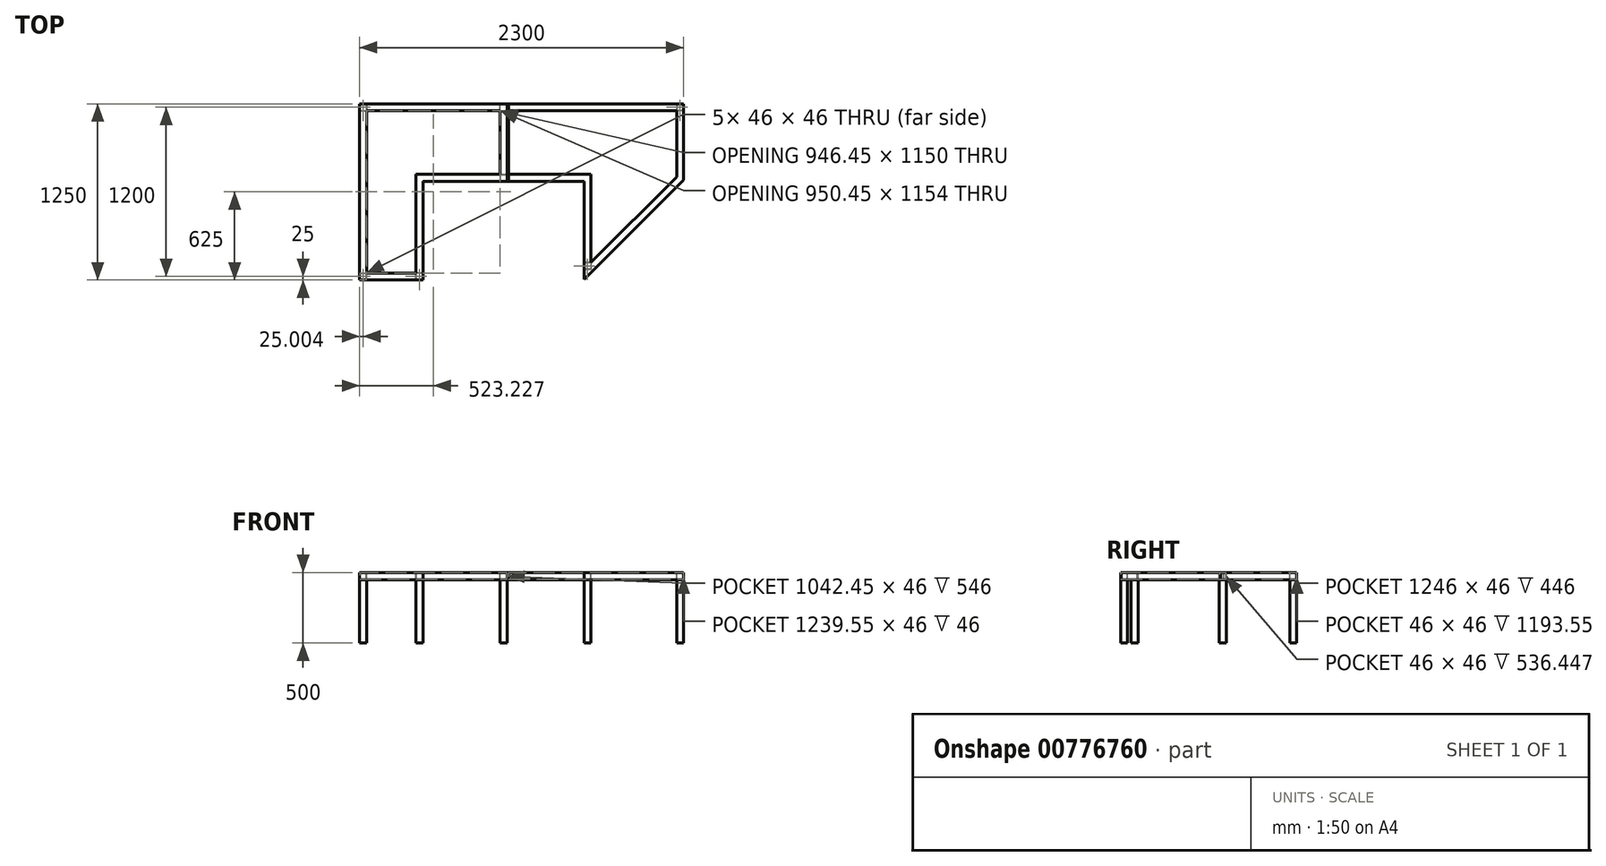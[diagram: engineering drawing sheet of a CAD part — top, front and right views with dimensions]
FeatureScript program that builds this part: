
annotation { "Feature Type Name" : "Feature", "Feature Type Description" : "" }
export const myFeature = defineFeature(function(context is Context, id is Id, definition is map)
    precondition{}
    {
        {
            var Q0;
            Q0=qCreatedBy(makeId("Top.planeOp"),FACE);
            var sketch = newSketch(context, id + "F0", { "sketchPlane" : qUnion([Q0])});
            skLineSegment(sketch, "E0.top", {"start": v(-571.45, -975) * mm, "end": v(-1021.45, -975) * mm});
            skLineSegment(sketch, "E0.left", {"start": v(-571.45, -275) * mm, "end": v(-571.45, -975) * mm});
            skLineSegment(sketch, "E0.right", {"start": v(-1021.45, 275) * mm, "end": v(-1021.45, -975) * mm});
            skLineSegment(sketch, "E1.right", {"start": v(1278.55, 275) * mm, "end": v(1278.55, -265) * mm});
            skLineSegment(sketch, "E2", {"start": v(1278.55, -265) * mm, "end": v(571.45, -972.1) * mm});
            skLineSegment(sketch, "E3", {"start": v(571.45, -972.1) * mm, "end": v(571.45, -275) * mm});
            skLineSegment(sketch, "E4", {"start": v(1278.55, 275) * mm, "end": v(-1021.45, 275) * mm});
            skLineSegment(sketch, "E5", {"start": v(-571.45, -275) * mm, "end": v(571.45, -275) * mm});
            skLineSegment(sketch, "E6", {"start": v(35, -275) * mm, "end": v(35, 275) * mm});
            skLineSegment(sketch, "E7", {"start": v(0, 250) * mm, "end": v(0, -250) * mm, "construction": true});
            skLineSegment(sketch, "E8", {"start": v(25, 275) * mm, "end": v(25, -275) * mm});
            skLineSegment(sketch, "E9.0", {"start": v(621.45, -851.4) * mm, "end": v(621.45, -225) * mm});
            skLineSegment(sketch, "E9.1", {"start": v(1228.55, -244.29) * mm, "end": v(621.45, -851.4) * mm});
            skLineSegment(sketch, "E9.2", {"start": v(1228.55, 225) * mm, "end": v(1228.55, -244.29) * mm});
            skLineSegment(sketch, "E10.0", {"start": v(-621.45, -225) * mm, "end": v(-621.45, -925) * mm});
            skLineSegment(sketch, "E10.1", {"start": v(-621.45, -925) * mm, "end": v(-971.45, -925) * mm});
            skLineSegment(sketch, "E10.2", {"start": v(-971.45, 225) * mm, "end": v(-971.45, -925) * mm});
            skLineSegment(sketch, "E11", {"start": v(1228.55, 225) * mm, "end": v(35, 225) * mm});
            skLineSegment(sketch, "E12", {"start": v(35, -225) * mm, "end": v(621.45, -225) * mm});
            skLineSegment(sketch, "E13", {"start": v(-621.45, -225) * mm, "end": v(-25, -225) * mm});
            skLineSegment(sketch, "E14", {"start": v(-25, -225) * mm, "end": v(-25, 225) * mm});
            skLineSegment(sketch, "E15.trimOffspring", {"start": v(-25, 225) * mm, "end": v(-971.45, 225) * mm});
            skLineSegment(sketch, "E16", {"start": v(25, 275) * mm, "end": v(-25, 225) * mm});
            skLineSegment(sketch, "E17", {"start": v(-25, -225) * mm, "end": v(25, -275) * mm});
            skLineSegment(sketch, "E18", {"start": v(-621.45, -925) * mm, "end": v(-571.45, -975) * mm});
            skLineSegment(sketch, "E19", {"start": v(-971.45, -925) * mm, "end": v(-1021.45, -975) * mm});
            skLineSegment(sketch, "E20", {"start": v(-571.45, -275) * mm, "end": v(-621.45, -225) * mm});
            skLineSegment(sketch, "E21", {"start": v(-971.45, 225) * mm, "end": v(-1021.45, 275) * mm});
            skLineSegment(sketch, "E22", {"start": v(621.45, -225) * mm, "end": v(571.45, -275) * mm});
            skLineSegment(sketch, "E23", {"start": v(621.45, -851.4) * mm, "end": v(571.45, -901.4) * mm});
            skLineSegment(sketch, "E24", {"start": v(1278.55, -265) * mm, "end": v(1228.55, -244.29) * mm});
            skLineSegment(sketch, "E25", {"start": v(1278.55, 275) * mm, "end": v(1228.55, 225) * mm});
            skSolve(sketch);
        }
        {
            var Q0;
            {var subQ4=sQuery(id+"F0.wireOp",EDGE,"E11");Q0=makeQuery(id+"F0.imprint","IMPRINT",FACE,{"disambiguationData":[TD([[makeQuery(id+"F0.imprint","IMPRINT",EDGE,{"derivedFrom":subQ4}),-1.0]])]});}
            var Q1;
            {var subQ4=sQuery(id+"F0.wireOp",EDGE,"E12");Q1=makeQuery(id+"F0.imprint","IMPRINT",FACE,{"disambiguationData":[TD([[makeQuery(id+"F0.imprint","IMPRINT",EDGE,{"derivedFrom":subQ4}),-1.0]])]});}
            var Q2;
            Q2=makeQuery(id+"F0.imprint","IMPRINT",FACE,{"disambiguationData":[TD([[makeQuery(id+"F0.imprint","IMPRINT",EDGE,{"derivedFrom":sQuery(id+"F0.wireOp",EDGE,"E1.right")}),-1.0]])]});
            var Q3;
            {var subQ2=sQuery(id+"F0.wireOp",EDGE,"E2");Q3=makeQuery(id+"F0.imprint","IMPRINT",FACE,{"disambiguationData":[TD([[makeQuery(id+"F0.imprint","IMPRINT",EDGE,{"derivedFrom":subQ2}),-1.0]])]});}
            var Q4;
            Q4=makeQuery(id+"F0.imprint","IMPRINT",FACE,{"disambiguationData":[TD([[makeQuery(id+"F0.imprint","IMPRINT",EDGE,{"derivedFrom":sQuery(id+"F0.wireOp",EDGE,"E9.0")}),1.0]])]});
            extrude(context, id + "F1", {"entities" : qUnion([Q0, Q1, Q2, Q3, Q4]), "oppositeDirection" : true, "depth" : 50 * mm, "offsetDistance" : 25 * mm});
        }
        {
            var Q0;
            Q0=makeQuery(id+"F0.imprint","IMPRINT",FACE,{"disambiguationData":[TD([[makeQuery(id+"F0.imprint","IMPRINT",EDGE,{"derivedFrom":sQuery(id+"F0.wireOp",EDGE,"E0.right")}),1.0]])]});
            var Q1;
            Q1=makeQuery(id+"F0.imprint","IMPRINT",FACE,{"disambiguationData":[TD([[makeQuery(id+"F0.imprint","IMPRINT",EDGE,{"derivedFrom":sQuery(id+"F0.wireOp",EDGE,"E0.top")}),-1.0]])]});
            var Q2;
            Q2=makeQuery(id+"F0.imprint","IMPRINT",FACE,{"disambiguationData":[TD([[makeQuery(id+"F0.imprint","IMPRINT",EDGE,{"derivedFrom":sQuery(id+"F0.wireOp",EDGE,"E0.left")}),-1.0]])]});
            var Q3;
            Q3=makeQuery(id+"F0.imprint","IMPRINT",FACE,{"disambiguationData":[TD([[makeQuery(id+"F0.imprint","IMPRINT",EDGE,{"derivedFrom":sQuery(id+"F0.wireOp",EDGE,"E15.trimOffspring")}),-1.0]])]});
            var Q4;
            Q4=makeQuery(id+"F0.imprint","IMPRINT",FACE,{"disambiguationData":[TD([[makeQuery(id+"F0.imprint","IMPRINT",EDGE,{"derivedFrom":sQuery(id+"F0.wireOp",EDGE,"E13")}),-1.0]])]});
            var Q5;
            Q5=makeQuery(id+"F0.imprint","IMPRINT",FACE,{"disambiguationData":[TD([[makeQuery(id+"F0.imprint","IMPRINT",EDGE,{"derivedFrom":sQuery(id+"F0.wireOp",EDGE,"E8")}),-1.0]])]});
            extrude(context, id + "F2", {"entities" : qUnion([Q0, Q1, Q2, Q3, Q4, Q5]), "oppositeDirection" : true, "depth" : 50 * mm, "offsetDistance" : 25 * mm});
        }
        {
            var Q0;
            {var subQ5=sQuery(id+"F0.wireOp",EDGE,"E8");Q0=makeQuery(id+"F0.imprint","IMPRINT",FACE,{"disambiguationData":[TD([[makeQuery(id+"F0.imprint","IMPRINT",EDGE,{"derivedFrom":subQ5}),1.0]])]});}
            extrude(context, id + "F3", {"entities" : qUnion([Q0]), "oppositeDirection" : true, "depth" : 50 * mm, "offsetDistance" : 25 * mm});
        }
        {
            var Q0;
            Q0=makeQuery(id+"F2.opExtrude","SWEPT_FACE",FACE,{"disambiguationData":[OSD([sQuery(id+"F0.wireOp",EDGE,"2A5xBHzc-K11I-RF4C-uFUW-yK5MyYlXpvJs")])]});
            var Q1;
            Q1=makeQuery(id+"F2.opExtrude","SWEPT_FACE",FACE,{"disambiguationData":[OSD([sQuery(id+"F0.wireOp",EDGE,"euzSzvIf-zb11-oeAi-6vT1-MCLPW0OJACnm")])]});
            var Q2;
            Q2=makeQuery(id+"F2.opExtrude","SWEPT_FACE",FACE,{"disambiguationData":[OSD([sQuery(id+"F0.wireOp",EDGE,"GaZW1oPM-7css-87Zt-WlsF-Pj7CSG2FI9am")])]});
            var Q3;
            Q3=makeQuery(id+"F2.opExtrude","SWEPT_FACE",FACE,{"disambiguationData":[OSD([sQuery(id+"F0.wireOp",EDGE,"sEP72Xz7-jys3-R5h0-IGae-Pih6YAF2AQWA")])]});
            var Q4;
            Q4=makeQuery(id+"F2.opExtrude","SWEPT_FACE",FACE,{"disambiguationData":[OSD([sQuery(id+"F0.wireOp",EDGE,"c1XjSD7W-lne4-ik7T-Z6My-GW0DLpmjkOK7")])]});
            var Q5;
            Q5=makeQuery(id+"F2.opExtrude","SWEPT_FACE",FACE,{"disambiguationData":[OSD([sQuery(id+"F0.wireOp",EDGE,"E3")])]});
            var Q6;
            Q6=makeQuery(id+"F2.opExtrude","SWEPT_FACE",FACE,{"disambiguationData":[OSD([sQuery(id+"F0.wireOp",EDGE,"Wdln1U8m-EFWw-qeqF-QT6C-txq9QpAb5bMw")])]});
            var Q7;
            Q7=makeQuery(id+"F2.opExtrude","SWEPT_FACE",FACE,{"disambiguationData":[OSD([sQuery(id+"F0.wireOp",EDGE,"AmBgJv7p-42l0-yFrp-UsyM-nx3i3Yf4QRB6")])]});
            var Q8;
            Q8=makeQuery(id+"F2.opExtrude","SWEPT_FACE",FACE,{"disambiguationData":[OSD([sQuery(id+"F0.wireOp",EDGE,"OMlm4TEm-4dLt-MTcu-9hLO-nY8Iuq9vEE24")])]});
            var Q9;
            Q9=makeQuery(id+"F2.opExtrude","SWEPT_FACE",FACE,{"disambiguationData":[OSD([sQuery(id+"F0.wireOp",EDGE,"wsWtQ9dq-29bv-YeLY-ytrv-cSZXrYwj46Cy")])]});
            var Q10;
            Q10=makeQuery(id+"F2.opExtrude","SWEPT_FACE",FACE,{"disambiguationData":[OSD([sQuery(id+"F0.wireOp",EDGE,"UwJ4Ktt8-JkZr-7fMy-kYLK-IwmRaqzIre9T")])]});
            var Q11;
            Q11=makeQuery(id+"F2.opExtrude","SWEPT_FACE",FACE,{"disambiguationData":[OSD([sQuery(id+"F0.wireOp",EDGE,"jgCBQ05M-ki6p-DAOy-uykI-KBMVmP0mj9T2")])]});
            var Q12;
            Q12=makeQuery(id+"F2.opExtrude","SWEPT_BODY",BODY,{"disambiguationData":[OSD([sQuery(id+"F0.wireOp",EDGE,"E0.top"),sQuery(id+"F0.wireOp",EDGE,"E0.left"),sQuery(id+"F0.wireOp",EDGE,"E0.right"),sQuery(id+"F0.wireOp",EDGE,"E4"),sQuery(id+"F0.wireOp",EDGE,"E5"),sQuery(id+"F0.wireOp",EDGE,"E8"),sQuery(id+"F0.wireOp",EDGE,"E10.0"),sQuery(id+"F0.wireOp",EDGE,"E10.1"),sQuery(id+"F0.wireOp",EDGE,"E10.2"),sQuery(id+"F0.wireOp",EDGE,"E13"),sQuery(id+"F0.wireOp",EDGE,"E14"),sQuery(id+"F0.wireOp",EDGE,"E15.trimOffspring")])]});
            var Q13;
            Q13=makeQuery(id+"F1.opExtrude","SWEPT_BODY",BODY,{"disambiguationData":[OSD([sQuery(id+"F0.wireOp",EDGE,"E1.right"),sQuery(id+"F0.wireOp",EDGE,"E2"),sQuery(id+"F0.wireOp",EDGE,"E3"),sQuery(id+"F0.wireOp",EDGE,"E4"),sQuery(id+"F0.wireOp",EDGE,"E5"),sQuery(id+"F0.wireOp",EDGE,"E6"),sQuery(id+"F0.wireOp",EDGE,"E9.0"),sQuery(id+"F0.wireOp",EDGE,"E9.1"),sQuery(id+"F0.wireOp",EDGE,"E9.2"),sQuery(id+"F0.wireOp",EDGE,"E11"),sQuery(id+"F0.wireOp",EDGE,"E12")])]});
            shell(context, id + "F4", {"isHollow" : true, "entities" : qUnion([Q0, Q1, Q2, Q3, Q4, Q5, Q6, Q7, Q8, Q9, Q10, Q11]), "parts" : qUnion([Q12, Q13]), "thickness" : 2 * mm});
        }
        {
            var Q0;
            Q0=makeQuery(id+"F1.opExtrude","CAP_FACE",FACE,{"disambiguationData":[OSD([sQuery(id+"F0.wireOp",EDGE,"E0.top"),sQuery(id+"F0.wireOp",EDGE,"E0.left"),sQuery(id+"F0.wireOp",EDGE,"E0.right"),sQuery(id+"F0.wireOp",EDGE,"E1.bottom"),sQuery(id+"F0.wireOp",EDGE,"E1.right"),sQuery(id+"F0.wireOp",EDGE,"E2"),sQuery(id+"F0.wireOp",EDGE,"E3"),sQuery(id+"F0.wireOp",EDGE,"E4"),sQuery(id+"F0.wireOp",EDGE,"3MHuuK1R-XM8M-TEry-PjCO-C2Ca8WDOHeh9"),sQuery(id+"F0.wireOp",EDGE,"E5"),sQuery(id+"F0.wireOp",EDGE,"ef3f4d72-5e47-419f-9294-d8863ce435e2.0"),sQuery(id+"F0.wireOp",EDGE,"ef3f4d72-5e47-419f-9294-d8863ce435e2.1"),sQuery(id+"F0.wireOp",EDGE,"ef3f4d72-5e47-419f-9294-d8863ce435e2.2"),sQuery(id+"F0.wireOp",EDGE,"ef3f4d72-5e47-419f-9294-d8863ce435e2.3"),sQuery(id+"F0.wireOp",EDGE,"ef3f4d72-5e47-419f-9294-d8863ce435e2.4"),sQuery(id+"F0.wireOp",EDGE,"ef3f4d72-5e47-419f-9294-d8863ce435e2.5"),sQuery(id+"F0.wireOp",EDGE,"93901ade-92e2-49f1-bb5c-9fd08a6a9788.0"),sQuery(id+"F0.wireOp",EDGE,"93901ade-92e2-49f1-bb5c-9fd08a6a9788.1"),sQuery(id+"F0.wireOp",EDGE,"93901ade-92e2-49f1-bb5c-9fd08a6a9788.2"),sQuery(id+"F0.wireOp",EDGE,"93901ade-92e2-49f1-bb5c-9fd08a6a9788.3"),sQuery(id+"F0.wireOp",EDGE,"93901ade-92e2-49f1-bb5c-9fd08a6a9788.4"),sQuery(id+"F0.wireOp",EDGE,"93901ade-92e2-49f1-bb5c-9fd08a6a9788.5")])],"isStart":false});
            var sketch = newSketch(context, id + "F5", { "sketchPlane" : qUnion([Q0])});
            skLineSegment(sketch, "E26.bottom", {"start": v(-1021.45, 975) * mm, "end": v(-971.45, 975) * mm});
            skLineSegment(sketch, "E26.top", {"start": v(-1021.45, 925) * mm, "end": v(-971.45, 925) * mm});
            skLineSegment(sketch, "E26.left", {"start": v(-1021.45, 975) * mm, "end": v(-1021.45, 925) * mm});
            skLineSegment(sketch, "E26.right", {"start": v(-971.45, 975) * mm, "end": v(-971.45, 925) * mm});
            skLineSegment(sketch, "E27.bottom", {"start": v(-1021.45, -275) * mm, "end": v(-971.45, -275) * mm});
            skLineSegment(sketch, "E27.top", {"start": v(-1021.45, -225) * mm, "end": v(-971.45, -225) * mm});
            skLineSegment(sketch, "E27.left", {"start": v(-1021.45, -275) * mm, "end": v(-1021.45, -225) * mm});
            skLineSegment(sketch, "E27.right", {"start": v(-971.45, -275) * mm, "end": v(-971.45, -225) * mm});
            skLineSegment(sketch, "E28.bottom", {"start": v(1278.55, -275) * mm, "end": v(1228.55, -275) * mm});
            skLineSegment(sketch, "E28.top", {"start": v(1278.55, -225) * mm, "end": v(1228.55, -225) * mm});
            skLineSegment(sketch, "E28.left", {"start": v(1278.55, -275) * mm, "end": v(1278.55, -225) * mm});
            skLineSegment(sketch, "E28.right", {"start": v(1228.55, -275) * mm, "end": v(1228.55, -225) * mm});
            skLineSegment(sketch, "E29.bottom", {"start": v(621.45, 851.4) * mm, "end": v(571.45, 851.4) * mm});
            skLineSegment(sketch, "E29.top", {"start": v(621.45, 901.4) * mm, "end": v(571.45, 901.4) * mm});
            skLineSegment(sketch, "E29.left", {"start": v(621.45, 851.4) * mm, "end": v(621.45, 901.4) * mm});
            skLineSegment(sketch, "E29.right", {"start": v(571.45, 851.4) * mm, "end": v(571.45, 901.4) * mm});
            skPoint(sketch, "E30.0", {"position": v(-971.45, 925) * mm});
            skPoint(sketch, "E31.0", {"position": v(-1021.45, 975) * mm});
            skPoint(sketch, "E32.0", {"position": v(-1021.45, -275) * mm});
            skPoint(sketch, "E33.0", {"position": v(-971.45, -225) * mm});
            skPoint(sketch, "E34.0", {"position": v(-571.45, 975) * mm});
            skPoint(sketch, "E35.0", {"position": v(-621.45, 925) * mm});
            skLineSegment(sketch, "E36.bottom", {"start": v(-571.45, 975) * mm, "end": v(-621.45, 975) * mm});
            skLineSegment(sketch, "E36.top", {"start": v(-571.45, 925) * mm, "end": v(-621.45, 925) * mm});
            skLineSegment(sketch, "E36.left", {"start": v(-571.45, 975) * mm, "end": v(-571.45, 925) * mm});
            skLineSegment(sketch, "E36.right", {"start": v(-621.45, 975) * mm, "end": v(-621.45, 925) * mm});
            skPoint(sketch, "E37.0", {"position": v(1228.55, -225) * mm});
            skPoint(sketch, "E38.0", {"position": v(1278.55, -275) * mm});
            skPoint(sketch, "E39.0", {"position": v(621.45, 851.4) * mm});
            skLineSegment(sketch, "E40.0", {"start": v(571.45, 972.1) * mm, "end": v(571.45, 275) * mm, "construction": true});
            skPoint(sketch, "E41.0", {"position": v(-25, 225) * mm});
            skPoint(sketch, "E42.0", {"position": v(25, 275) * mm});
            skPoint(sketch, "E43.0", {"position": v(-25, -225) * mm});
            skPoint(sketch, "E44.0", {"position": v(25, -275) * mm});
            skLineSegment(sketch, "E45.bottom", {"start": v(-25, 225) * mm, "end": v(25, 225) * mm});
            skLineSegment(sketch, "E45.top", {"start": v(-25, 275) * mm, "end": v(25, 275) * mm});
            skLineSegment(sketch, "E45.left", {"start": v(-25, 225) * mm, "end": v(-25, 275) * mm});
            skLineSegment(sketch, "E45.right", {"start": v(25, 225) * mm, "end": v(25, 275) * mm});
            skLineSegment(sketch, "E46.bottom", {"start": v(-25, -225) * mm, "end": v(25, -225) * mm});
            skLineSegment(sketch, "E46.top", {"start": v(-25, -275) * mm, "end": v(25, -275) * mm});
            skLineSegment(sketch, "E46.left", {"start": v(-25, -225) * mm, "end": v(-25, -275) * mm});
            skLineSegment(sketch, "E46.right", {"start": v(25, -225) * mm, "end": v(25, -275) * mm});
            skSolve(sketch);
        }
        {
            var Q0;
            Q0 = qSketchRegion(id + "F5", true);
            extrude(context, id + "F6", {"entities" : qUnion([Q0]), "depth" : 450 * mm, "offsetDistance" : 25 * mm});
        }
        {
            var Q0;
            Q0=makeQuery(id+"F6.opExtrude","CAP_FACE",FACE,{"disambiguationData":[OSD([sQuery(id+"F5.wireOp",EDGE,"E27.bottom"),sQuery(id+"F5.wireOp",EDGE,"E27.top"),sQuery(id+"F5.wireOp",EDGE,"E27.left"),sQuery(id+"F5.wireOp",EDGE,"E27.right")])],"isStart":true});
            var Q1;
            Q1=makeQuery(id+"F6.opExtrude","CAP_FACE",FACE,{"disambiguationData":[OSD([sQuery(id+"F5.wireOp",EDGE,"E26.bottom"),sQuery(id+"F5.wireOp",EDGE,"E26.top"),sQuery(id+"F5.wireOp",EDGE,"E26.left"),sQuery(id+"F5.wireOp",EDGE,"E26.right")])],"isStart":true});
            var Q2;
            Q2=makeQuery(id+"F6.opExtrude","CAP_FACE",FACE,{"disambiguationData":[OSD([sQuery(id+"F5.wireOp",EDGE,"E26.bottom"),sQuery(id+"F5.wireOp",EDGE,"E26.top"),sQuery(id+"F5.wireOp",EDGE,"E26.left"),sQuery(id+"F5.wireOp",EDGE,"E26.right")])],"isStart":false});
            var Q3;
            Q3=makeQuery(id+"F6.opExtrude","CAP_FACE",FACE,{"disambiguationData":[OSD([sQuery(id+"F5.wireOp",EDGE,"E27.bottom"),sQuery(id+"F5.wireOp",EDGE,"E27.top"),sQuery(id+"F5.wireOp",EDGE,"E27.left"),sQuery(id+"F5.wireOp",EDGE,"E27.right")])],"isStart":false});
            var Q4;
            Q4=makeQuery(id+"F6.opExtrude","CAP_FACE",FACE,{"disambiguationData":[OSD([sQuery(id+"F5.wireOp",EDGE,"E29.bottom"),sQuery(id+"F5.wireOp",EDGE,"E29.top"),sQuery(id+"F5.wireOp",EDGE,"E29.left"),sQuery(id+"F5.wireOp",EDGE,"E29.right")])],"isStart":false});
            var Q5;
            Q5=makeQuery(id+"F6.opExtrude","CAP_FACE",FACE,{"disambiguationData":[OSD([sQuery(id+"F5.wireOp",EDGE,"E28.bottom"),sQuery(id+"F5.wireOp",EDGE,"E28.top"),sQuery(id+"F5.wireOp",EDGE,"E28.left"),sQuery(id+"F5.wireOp",EDGE,"E28.right")])],"isStart":false});
            var Q6;
            Q6=makeQuery(id+"F6.opExtrude","CAP_FACE",FACE,{"disambiguationData":[OSD([sQuery(id+"F5.wireOp",EDGE,"E29.bottom"),sQuery(id+"F5.wireOp",EDGE,"E29.top"),sQuery(id+"F5.wireOp",EDGE,"E29.left"),sQuery(id+"F5.wireOp",EDGE,"E29.right")])],"isStart":true});
            var Q7;
            Q7=makeQuery(id+"F6.opExtrude","CAP_FACE",FACE,{"disambiguationData":[OSD([sQuery(id+"F5.wireOp",EDGE,"E28.bottom"),sQuery(id+"F5.wireOp",EDGE,"E28.top"),sQuery(id+"F5.wireOp",EDGE,"E28.left"),sQuery(id+"F5.wireOp",EDGE,"E28.right")])],"isStart":true});
            var Q8;
            Q8=makeQuery(id+"F6.opExtrude","CAP_FACE",FACE,{"disambiguationData":[OSD([sQuery(id+"F5.wireOp",EDGE,"E36.bottom"),sQuery(id+"F5.wireOp",EDGE,"E36.top"),sQuery(id+"F5.wireOp",EDGE,"E36.left"),sQuery(id+"F5.wireOp",EDGE,"E36.right")])],"isStart":false});
            var Q9;
            Q9=makeQuery(id+"F6.opExtrude","CAP_FACE",FACE,{"disambiguationData":[OSD([sQuery(id+"F5.wireOp",EDGE,"E36.bottom"),sQuery(id+"F5.wireOp",EDGE,"E36.top"),sQuery(id+"F5.wireOp",EDGE,"E36.left"),sQuery(id+"F5.wireOp",EDGE,"E36.right")])],"isStart":true});
            var Q10;
            Q10=makeQuery(id+"F6.opExtrude","CAP_FACE",FACE,{"disambiguationData":[OSD([sQuery(id+"F5.wireOp",EDGE,"E45.bottom"),sQuery(id+"F5.wireOp",EDGE,"E45.top"),sQuery(id+"F5.wireOp",EDGE,"E45.left"),sQuery(id+"F5.wireOp",EDGE,"E45.right")])],"isStart":false});
            var Q11;
            Q11=makeQuery(id+"F6.opExtrude","CAP_FACE",FACE,{"disambiguationData":[OSD([sQuery(id+"F5.wireOp",EDGE,"E46.bottom"),sQuery(id+"F5.wireOp",EDGE,"E46.top"),sQuery(id+"F5.wireOp",EDGE,"E46.left"),sQuery(id+"F5.wireOp",EDGE,"E46.right")])],"isStart":false});
            shell(context, id + "F7", {"entities" : qUnion([Q0, Q1, Q2, Q3, Q4, Q5, Q6, Q7, Q8, Q9, Q10, Q11]), "thickness" : 2 * mm});
        }
    });
